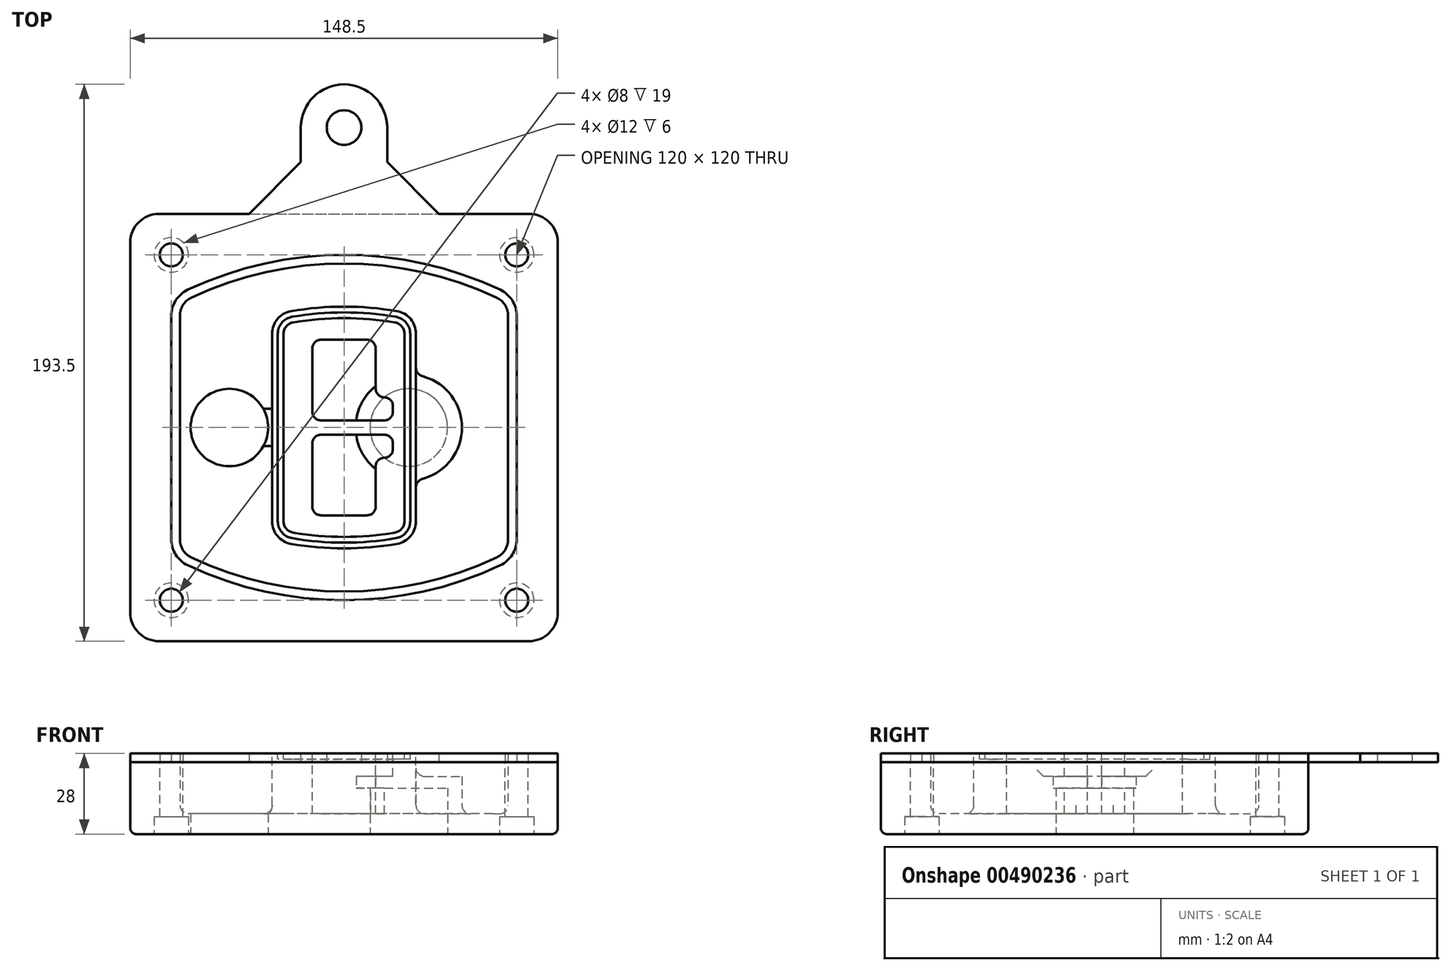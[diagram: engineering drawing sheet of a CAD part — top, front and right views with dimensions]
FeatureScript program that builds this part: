
annotation { "Feature Type Name" : "Feature", "Feature Type Description" : "" }
export const myFeature = defineFeature(function(context is Context, id is Id, definition is map)
    precondition{}
    {
        {
            var Q0;
            Q0=qCreatedBy(makeId("Top.planeOp"),FACE);
            var sketch = newSketch(context, id + "F0", { "sketchPlane" : qUnion([Q0])});
            skPoint(sketch, "E0.rect.middle", {"position": v(0, 0) * mm});
            skLineSegment(sketch, "E1.bottom", {"start": v(-64.25, -74.25) * mm, "end": v(64.25, -74.25) * mm});
            skLineSegment(sketch, "E1.top", {"start": v(-64.25, 74.25) * mm, "end": v(64.25, 74.25) * mm});
            skLineSegment(sketch, "E1.left", {"start": v(-74.25, -64.25) * mm, "end": v(-74.25, 64.25) * mm});
            skLineSegment(sketch, "E1.right", {"start": v(74.25, -64.25) * mm, "end": v(74.25, 64.25) * mm});
            skLineSegment(sketch, "E2", {"start": v(-74.25, 74.25) * mm, "end": v(74.25, -74.25) * mm, "construction": true});
            skLineSegment(sketch, "E3", {"start": v(74.25, 74.25) * mm, "end": v(-74.25, -74.25) * mm, "construction": true});
            skCircle(sketch, "E4", {"center": v(-60, 60) * mm, "radius": 4 * mm});
            skCircle(sketch, "E5", {"center": v(60, 60) * mm, "radius": 4 * mm});
            skCircle(sketch, "E6", {"center": v(60, -60) * mm, "radius": 4 * mm});
            skCircle(sketch, "E7", {"center": v(-60, -60) * mm, "radius": 4 * mm});
            skLineSegment(sketch, "E8", {"start": v(-60, 60) * mm, "end": v(60, 60) * mm, "construction": true});
            skLineSegment(sketch, "E9", {"start": v(60, 60) * mm, "end": v(60, -60) * mm, "construction": true});
            skLineSegment(sketch, "E10", {"start": v(60, -60) * mm, "end": v(-60, -60) * mm, "construction": true});
            skLineSegment(sketch, "E11", {"start": v(-60, -60) * mm, "end": v(-60, 60) * mm, "construction": true});
            skLineSegment(sketch, "E12", {"start": v(-60, 38.83) * mm, "end": v(-60, -38.83) * mm});
            skLineSegment(sketch, "E13", {"start": v(60, 38.83) * mm, "end": v(60, -38.83) * mm});
            skArc(sketch, "E14", {"start": v(54.26, 47.88) * mm, "mid": v(0, 60) * mm, "end": v(-54.26, 47.88) * mm});
            skArc(sketch, "E15", {"start": v(-54.26, -47.88) * mm, "mid": v(0, -60) * mm, "end": v(54.26, -47.88) * mm});
            skLineSegment(sketch, "E16", {"start": v(-60, 0) * mm, "end": v(60, 0) * mm, "construction": true});
            skPoint(sketch, "E17.visualSharp", {"position": v(-60, -45) * mm});
            skArc(sketch, "E17.filletArc", {"start": v(-60, -38.83) * mm, "mid": v(-58.44, -44.2) * mm, "end": v(-54.26, -47.88) * mm});
            skPoint(sketch, "E18.visualSharp", {"position": v(-60, 45) * mm});
            skArc(sketch, "E18.filletArc", {"start": v(-54.26, 47.88) * mm, "mid": v(-58.44, 44.2) * mm, "end": v(-60, 38.83) * mm});
            skPoint(sketch, "E19.visualSharp", {"position": v(60, 45) * mm});
            skArc(sketch, "E19.filletArc", {"start": v(60, 38.83) * mm, "mid": v(58.44, 44.2) * mm, "end": v(54.26, 47.88) * mm});
            skPoint(sketch, "E20.visualSharp", {"position": v(60, -45) * mm});
            skArc(sketch, "E20.filletArc", {"start": v(54.26, -47.88) * mm, "mid": v(58.44, -44.2) * mm, "end": v(60, -38.83) * mm});
            skPoint(sketch, "E21.visualSharp", {"position": v(-74.25, 74.25) * mm});
            skArc(sketch, "E21.filletArc", {"start": v(-64.25, 74.25) * mm, "mid": v(-71.32, 71.32) * mm, "end": v(-74.25, 64.25) * mm});
            skPoint(sketch, "E22.visualSharp", {"position": v(74.25, 74.25) * mm});
            skArc(sketch, "E22.filletArc", {"start": v(74.25, 64.25) * mm, "mid": v(71.32, 71.32) * mm, "end": v(64.25, 74.25) * mm});
            skPoint(sketch, "E23.visualSharp", {"position": v(74.25, -74.25) * mm});
            skArc(sketch, "E23.filletArc", {"start": v(64.25, -74.25) * mm, "mid": v(71.32, -71.32) * mm, "end": v(74.25, -64.25) * mm});
            skPoint(sketch, "E24.visualSharp", {"position": v(-74.25, -74.25) * mm});
            skArc(sketch, "E24.filletArc", {"start": v(-74.25, -64.25) * mm, "mid": v(-71.32, -71.32) * mm, "end": v(-64.25, -74.25) * mm});
            skArc(sketch, "E25.0", {"start": v(57, 38.83) * mm, "mid": v(55.9, 42.58) * mm, "end": v(52.98, 45.17) * mm});
            skLineSegment(sketch, "E25.1", {"start": v(57, 38.83) * mm, "end": v(57, -38.83) * mm});
            skArc(sketch, "E25.2", {"start": v(52.98, -45.17) * mm, "mid": v(55.9, -42.58) * mm, "end": v(57, -38.83) * mm});
            skArc(sketch, "E25.3", {"start": v(-52.98, -45.17) * mm, "mid": v(0, -57) * mm, "end": v(52.98, -45.17) * mm});
            skArc(sketch, "E25.4", {"start": v(-57, -38.83) * mm, "mid": v(-55.9, -42.58) * mm, "end": v(-52.98, -45.17) * mm});
            skArc(sketch, "E25.5", {"start": v(52.98, 45.17) * mm, "mid": v(0, 57) * mm, "end": v(-52.98, 45.17) * mm});
            skLineSegment(sketch, "E25.6", {"start": v(-57, 38.83) * mm, "end": v(-57, -38.83) * mm});
            skArc(sketch, "E25.7", {"start": v(-52.98, 45.17) * mm, "mid": v(-55.9, 42.58) * mm, "end": v(-57, 38.83) * mm});
            skArc(sketch, "E26.0", {"start": v(-55.96, 51.5) * mm, "mid": v(-61.82, 46.33) * mm, "end": v(-64, 38.83) * mm});
            skArc(sketch, "E26.1", {"start": v(55.96, 51.5) * mm, "mid": v(0, 64) * mm, "end": v(-55.96, 51.5) * mm});
            skArc(sketch, "E26.2", {"start": v(64, 38.83) * mm, "mid": v(61.82, 46.33) * mm, "end": v(55.96, 51.5) * mm});
            skLineSegment(sketch, "E26.3", {"start": v(64, 38.83) * mm, "end": v(64, -38.83) * mm});
            skArc(sketch, "E26.4", {"start": v(55.96, -51.5) * mm, "mid": v(61.82, -46.33) * mm, "end": v(64, -38.83) * mm});
            skLineSegment(sketch, "E26.5", {"start": v(-64, 38.83) * mm, "end": v(-64, -38.83) * mm});
            skArc(sketch, "E26.6", {"start": v(-55.96, -51.5) * mm, "mid": v(0, -64) * mm, "end": v(55.96, -51.5) * mm});
            skArc(sketch, "E26.7", {"start": v(-64, -38.83) * mm, "mid": v(-61.82, -46.33) * mm, "end": v(-55.96, -51.5) * mm});
            skSolve(sketch);
        }
        {
            var Q0;
            Q0=makeQuery(id+"F0.imprint","IMPRINT",FACE,{"disambiguationData":[TD([[makeQuery(id+"F0.imprint","IMPRINT",EDGE,{"derivedFrom":sQuery(id+"F0.wireOp",EDGE,"E1.bottom")}),1.0]])]});
            var Q1;
            Q1=makeQuery(id+"F0.imprint","IMPRINT",FACE,{"disambiguationData":[TD([[makeQuery(id+"F0.imprint","IMPRINT",EDGE,{"derivedFrom":sQuery(id+"F0.wireOp",EDGE,"E12")}),1.0]])]});
            var Q2;
            Q2=makeQuery(id+"F0.imprint","IMPRINT",FACE,{"disambiguationData":[TD([[makeQuery(id+"F0.imprint","IMPRINT",EDGE,{"derivedFrom":sQuery(id+"F0.wireOp",EDGE,"E25.0")}),1.0]])]});
            var Q3;
            Q3=makeQuery(id+"F0.imprint","IMPRINT",FACE,{"disambiguationData":[TD([[makeQuery(id+"F0.imprint","IMPRINT",EDGE,{"derivedFrom":sQuery(id+"F0.wireOp",EDGE,"E12")}),-1.0]])]});
            extrude(context, id + "F1", {"entities" : qUnion([Q0, Q1, Q2, Q3]), "oppositeDirection" : true, "depth" : 25 * mm});
        }
        {
            var Q0;
            Q0=makeQuery(id+"F0.imprint","IMPRINT",FACE,{"disambiguationData":[TD([[makeQuery(id+"F0.imprint","IMPRINT",EDGE,{"derivedFrom":sQuery(id+"F0.wireOp",EDGE,"E12")}),1.0]])]});
            extrude(context, id + "F2", {"entities" : qUnion([Q0]), "operationType" : NewBodyOperationType.ADD, "depth" : 3 * mm});
        }
        {
            var Q0;
            Q0=makeQuery(id+"F0.imprint","IMPRINT",FACE,{"disambiguationData":[TD([[makeQuery(id+"F0.imprint","IMPRINT",EDGE,{"derivedFrom":sQuery(id+"F0.wireOp",EDGE,"E25.0")}),1.0]])]});
            extrude(context, id + "F3", {"entities" : qUnion([Q0]), "operationType" : NewBodyOperationType.REMOVE, "oppositeDirection" : true, "depth" : 18 * mm});
        }
        {
            var Q0;
            Q0=makeQuery(id+"F2.opExtrude","CAP_FACE",FACE,{"disambiguationData":[OSD([sQuery(id+"F0.wireOp",EDGE,"E12"),sQuery(id+"F0.wireOp",EDGE,"E13"),sQuery(id+"F0.wireOp",EDGE,"E14"),sQuery(id+"F0.wireOp",EDGE,"E15"),sQuery(id+"F0.wireOp",EDGE,"E17.filletArc"),sQuery(id+"F0.wireOp",EDGE,"E18.filletArc"),sQuery(id+"F0.wireOp",EDGE,"E19.filletArc"),sQuery(id+"F0.wireOp",EDGE,"E20.filletArc"),sQuery(id+"F0.wireOp",EDGE,"E25.0"),sQuery(id+"F0.wireOp",EDGE,"E25.1"),sQuery(id+"F0.wireOp",EDGE,"E25.2"),sQuery(id+"F0.wireOp",EDGE,"E25.3"),sQuery(id+"F0.wireOp",EDGE,"E25.4"),sQuery(id+"F0.wireOp",EDGE,"E25.5"),sQuery(id+"F0.wireOp",EDGE,"E25.6"),sQuery(id+"F0.wireOp",EDGE,"E25.7")])],"isStart":false});
            var sketch = newSketch(context, id + "F4", { "sketchPlane" : qUnion([Q0])});
            skArc(sketch, "E27.0", {"start": v(-18.34, -40.45) * mm, "mid": v(0, -42) * mm, "end": v(18.34, -40.45) * mm});
            skArc(sketch, "E28.0", {"start": v(18.34, 40.45) * mm, "mid": v(0, 42) * mm, "end": v(-18.34, 40.45) * mm});
            skLineSegment(sketch, "E29", {"start": v(-25, 32.57) * mm, "end": v(-25, -32.57) * mm});
            skLineSegment(sketch, "E30", {"start": v(25, 32.57) * mm, "end": v(25, -32.57) * mm});
            skLineSegment(sketch, "E31", {"start": v(-25, 39.1) * mm, "end": v(25, 39.1) * mm, "construction": true});
            skLineSegment(sketch, "E32", {"start": v(-25, -39.1) * mm, "end": v(25, -39.1) * mm, "construction": true});
            skPoint(sketch, "E33.visualSharp", {"position": v(-25, 39.1) * mm});
            skArc(sketch, "E33.filletArc", {"start": v(-18.34, 40.45) * mm, "mid": v(-23.11, 37.73) * mm, "end": v(-25, 32.57) * mm});
            skPoint(sketch, "E34.visualSharp", {"position": v(25, 39.1) * mm});
            skArc(sketch, "E34.filletArc", {"start": v(25, 32.57) * mm, "mid": v(23.11, 37.73) * mm, "end": v(18.34, 40.45) * mm});
            skPoint(sketch, "E35.visualSharp", {"position": v(25, -39.1) * mm});
            skArc(sketch, "E35.filletArc", {"start": v(18.34, -40.45) * mm, "mid": v(23.11, -37.73) * mm, "end": v(25, -32.57) * mm});
            skPoint(sketch, "E36.visualSharp", {"position": v(-25, -39.1) * mm});
            skArc(sketch, "E36.filletArc", {"start": v(-25, -32.57) * mm, "mid": v(-23.11, -37.73) * mm, "end": v(-18.34, -40.45) * mm});
            skArc(sketch, "E37.0", {"start": v(52.98, 45.17) * mm, "mid": v(0, 57) * mm, "end": v(-52.98, 45.17) * mm});
            skArc(sketch, "E37.1", {"start": v(-52.98, 45.17) * mm, "mid": v(-55.9, 42.58) * mm, "end": v(-57, 38.83) * mm});
            skLineSegment(sketch, "E37.2", {"start": v(-57, 38.83) * mm, "end": v(-57, -38.83) * mm});
            skArc(sketch, "E37.3", {"start": v(-57, -38.83) * mm, "mid": v(-55.9, -42.58) * mm, "end": v(-52.98, -45.17) * mm});
            skArc(sketch, "E37.4", {"start": v(-52.98, -45.17) * mm, "mid": v(0, -57) * mm, "end": v(52.98, -45.17) * mm});
            skArc(sketch, "E37.5", {"start": v(52.98, -45.17) * mm, "mid": v(55.9, -42.58) * mm, "end": v(57, -38.83) * mm});
            skLineSegment(sketch, "E37.6", {"start": v(57, 38.83) * mm, "end": v(57, -38.83) * mm});
            skArc(sketch, "E37.7", {"start": v(57, 38.83) * mm, "mid": v(55.9, 42.58) * mm, "end": v(52.98, 45.17) * mm});
            skLineSegment(sketch, "E38.0", {"start": v(23, 32.57) * mm, "end": v(23, -32.57) * mm});
            skArc(sketch, "E38.1", {"start": v(18, -38.48) * mm, "mid": v(21.58, -36.44) * mm, "end": v(23, -32.57) * mm});
            skArc(sketch, "E38.2", {"start": v(-18, -38.48) * mm, "mid": v(0, -40) * mm, "end": v(18, -38.48) * mm});
            skArc(sketch, "E38.3", {"start": v(-23, -32.57) * mm, "mid": v(-21.58, -36.44) * mm, "end": v(-18, -38.48) * mm});
            skLineSegment(sketch, "E38.4", {"start": v(-23, 32.57) * mm, "end": v(-23, -32.57) * mm});
            skArc(sketch, "E38.5", {"start": v(23, 32.57) * mm, "mid": v(21.58, 36.44) * mm, "end": v(18, 38.48) * mm});
            skArc(sketch, "E38.6", {"start": v(-18, 38.48) * mm, "mid": v(-21.58, 36.44) * mm, "end": v(-23, 32.57) * mm});
            skArc(sketch, "E38.7", {"start": v(18, 38.48) * mm, "mid": v(0, 40) * mm, "end": v(-18, 38.48) * mm});
            skArc(sketch, "E39.0", {"start": v(21, 32.57) * mm, "mid": v(20.06, 35.15) * mm, "end": v(17.67, 36.5) * mm});
            skLineSegment(sketch, "E39.1", {"start": v(21, 32.57) * mm, "end": v(21, -32.57) * mm});
            skArc(sketch, "E39.2", {"start": v(17.67, -36.5) * mm, "mid": v(20.06, -35.15) * mm, "end": v(21, -32.57) * mm});
            skArc(sketch, "E39.3", {"start": v(-17.67, -36.5) * mm, "mid": v(0, -38) * mm, "end": v(17.67, -36.5) * mm});
            skArc(sketch, "E39.4", {"start": v(-21, -32.57) * mm, "mid": v(-20.06, -35.15) * mm, "end": v(-17.67, -36.5) * mm});
            skArc(sketch, "E39.5", {"start": v(17.67, 36.5) * mm, "mid": v(0, 38) * mm, "end": v(-17.67, 36.5) * mm});
            skLineSegment(sketch, "E39.6", {"start": v(-21, 32.57) * mm, "end": v(-21, -32.57) * mm});
            skArc(sketch, "E39.7", {"start": v(-17.67, 36.5) * mm, "mid": v(-20.06, 35.15) * mm, "end": v(-21, 32.57) * mm});
            skLineSegment(sketch, "E40", {"start": v(-25, 0) * mm, "end": v(25, 0) * mm, "construction": true});
            skLineSegment(sketch, "E41", {"start": v(-11, 5.5) * mm, "end": v(-11, 27.5) * mm});
            skLineSegment(sketch, "E42", {"start": v(-8, 30.5) * mm, "end": v(8, 30.5) * mm});
            skLineSegment(sketch, "E43", {"start": v(11, 27.5) * mm, "end": v(11, 13.5) * mm});
            skLineSegment(sketch, "E44", {"start": v(14, 10.5) * mm, "end": v(14, 10.5) * mm});
            skLineSegment(sketch, "E45", {"start": v(17, 7.5) * mm, "end": v(17, 5.5) * mm});
            skLineSegment(sketch, "E46", {"start": v(14, 2.5) * mm, "end": v(-8, 2.5) * mm});
            skPoint(sketch, "E47.visualSharp", {"position": v(-11, 30.5) * mm});
            skArc(sketch, "E47.filletArc", {"start": v(-8, 30.5) * mm, "mid": v(-10.12, 29.62) * mm, "end": v(-11, 27.5) * mm});
            skPoint(sketch, "E48.visualSharp", {"position": v(11, 30.5) * mm});
            skArc(sketch, "E48.filletArc", {"start": v(11, 27.5) * mm, "mid": v(10.12, 29.62) * mm, "end": v(8, 30.5) * mm});
            skPoint(sketch, "E49.visualSharp", {"position": v(11, 10.5) * mm});
            skArc(sketch, "E49.filletArc", {"start": v(11, 13.5) * mm, "mid": v(11.88, 11.38) * mm, "end": v(14, 10.5) * mm});
            skPoint(sketch, "E50.visualSharp", {"position": v(17, 10.5) * mm});
            skArc(sketch, "E50.filletArc", {"start": v(17, 7.5) * mm, "mid": v(16.12, 9.62) * mm, "end": v(14, 10.5) * mm});
            skPoint(sketch, "E51.visualSharp", {"position": v(17, 2.5) * mm});
            skArc(sketch, "E51.filletArc", {"start": v(14, 2.5) * mm, "mid": v(16.12, 3.38) * mm, "end": v(17, 5.5) * mm});
            skPoint(sketch, "E52.visualSharp", {"position": v(-11, 2.5) * mm});
            skArc(sketch, "E52.filletArc", {"start": v(-11, 5.5) * mm, "mid": v(-10.12, 3.38) * mm, "end": v(-8, 2.5) * mm});
            skLineSegment(sketch, "E53.0.MirrorCS", {"start": v(14, -2.5) * mm, "end": v(-8, -2.5) * mm});
            skArc(sketch, "E54.0.MirrorCS", {"start": v(-11, -5.5) * mm, "mid": v(-10.12, -3.38) * mm, "end": v(-8, -2.5) * mm});
            skLineSegment(sketch, "E55.0.MirrorCS", {"start": v(-11, -5.5) * mm, "end": v(-11, -27.5) * mm});
            skArc(sketch, "E56.0.MirrorCS", {"start": v(-8, -30.5) * mm, "mid": v(-10.12, -29.62) * mm, "end": v(-11, -27.5) * mm});
            skLineSegment(sketch, "E57.0.MirrorCS", {"start": v(-8, -30.5) * mm, "end": v(8, -30.5) * mm});
            skArc(sketch, "E58.0.MirrorCS", {"start": v(11, -27.5) * mm, "mid": v(10.12, -29.62) * mm, "end": v(8, -30.5) * mm});
            skLineSegment(sketch, "E59.0.MirrorCS", {"start": v(11, -27.5) * mm, "end": v(11, -13.5) * mm});
            skArc(sketch, "E60.0.MirrorCS", {"start": v(11, -13.5) * mm, "mid": v(11.88, -11.38) * mm, "end": v(14, -10.5) * mm});
            skArc(sketch, "E61.0.MirrorCS", {"start": v(17, -7.5) * mm, "mid": v(16.12, -9.62) * mm, "end": v(14, -10.5) * mm});
            skLineSegment(sketch, "E62.0.MirrorCS", {"start": v(17, -7.5) * mm, "end": v(17, -5.5) * mm});
            skArc(sketch, "E63.0.MirrorCS", {"start": v(14, -2.5) * mm, "mid": v(16.12, -3.38) * mm, "end": v(17, -5.5) * mm});
            skSolve(sketch);
        }
        {
            var Q0;
            Q0=makeQuery(id+"F4.imprint","IMPRINT",FACE,{"disambiguationData":[TD([[makeQuery(id+"F4.imprint","IMPRINT",EDGE,{"derivedFrom":sQuery(id+"F4.wireOp",EDGE,"E27.0")}),1.0]])]});
            var Q1;
            Q1=makeQuery(id+"F4.imprint","IMPRINT",FACE,{"disambiguationData":[TD([[makeQuery(id+"F4.imprint","IMPRINT",EDGE,{"derivedFrom":sQuery(id+"F4.wireOp",EDGE,"E38.0")}),-1.0]])]});
            var Q2;
            Q2=makeQuery(id+"F4.imprint","IMPRINT",FACE,{"disambiguationData":[TD([[makeQuery(id+"F4.imprint","IMPRINT",EDGE,{"derivedFrom":sQuery(id+"F4.wireOp",EDGE,"E39.0")}),1.0]])]});
            extrude(context, id + "F5", {"entities" : qUnion([Q0, Q1, Q2]), "operationType" : NewBodyOperationType.ADD, "endBound" : BoundingType.UP_TO_NEXT, "oppositeDirection" : true, "depth" : 25 * mm});
        }
        {
            var Q0;
            Q0=makeQuery(id+"F4.imprint","IMPRINT",FACE,{"disambiguationData":[TD([[makeQuery(id+"F4.imprint","IMPRINT",EDGE,{"derivedFrom":sQuery(id+"F4.wireOp",EDGE,"E38.0")}),-1.0]])]});
            extrude(context, id + "F6", {"entities" : qUnion([Q0]), "operationType" : NewBodyOperationType.REMOVE, "oppositeDirection" : true, "depth" : 2 * mm});
        }
        {
            var Q0;
            Q0=makeQuery(id+"F1.opExtrude","CAP_FACE",FACE,{"disambiguationData":[OSD([sQuery(id+"F0.wireOp",EDGE,"E1.bottom"),sQuery(id+"F0.wireOp",EDGE,"E1.top"),sQuery(id+"F0.wireOp",EDGE,"E1.left"),sQuery(id+"F0.wireOp",EDGE,"E1.right"),sQuery(id+"F0.wireOp",EDGE,"E4"),sQuery(id+"F0.wireOp",EDGE,"E5"),sQuery(id+"F0.wireOp",EDGE,"E6"),sQuery(id+"F0.wireOp",EDGE,"E7"),sQuery(id+"F0.wireOp",EDGE,"E21.filletArc"),sQuery(id+"F0.wireOp",EDGE,"E22.filletArc"),sQuery(id+"F0.wireOp",EDGE,"E23.filletArc"),sQuery(id+"F0.wireOp",EDGE,"E24.filletArc")])],"isStart":false});
            var sketch = newSketch(context, id + "F7", { "sketchPlane" : qUnion([Q0])});
            skCircle(sketch, "E64", {"center": v(22.5, 0) * mm, "radius": 13.47 * mm});
            skCircle(sketch, "E65", {"center": v(-39.81, 0) * mm, "radius": 13.47 * mm});
            skLineSegment(sketch, "E66", {"start": v(74.25, 0) * mm, "end": v(-74.25, 0) * mm});
            skCircle(sketch, "E67", {"center": v(22.5, 0) * mm, "radius": 18.47 * mm});
            skCircle(sketch, "E68", {"center": v(60, -60) * mm, "radius": 6 * mm});
            skCircle(sketch, "E69", {"center": v(-60, -60) * mm, "radius": 6 * mm});
            skCircle(sketch, "E70", {"center": v(-60, 60) * mm, "radius": 6 * mm});
            skCircle(sketch, "E71", {"center": v(60, 60) * mm, "radius": 6 * mm});
            skSolve(sketch);
        }
        {
            var Q0;
            {var subQ1=sQuery(id+"F7.wireOp",EDGE,"E66");var subQ4=sQuery(id+"F7.wireOp",EDGE,"E64");var subQ6=makeQuery(id+"F7.imprint","INTERSECT",VERTEX,{"disambiguationData":[OD(0.0)],"derivedFrom":[subQ4,subQ1]});Q0=makeQuery(id+"F7.imprint","IMPRINT",FACE,{"disambiguationData":[TD([[makeQuery(id+"F7.imprint","IMPRINT",EDGE,{"disambiguationData":[TD([[subQ6,-1.0]])],"derivedFrom":subQ4}),-1.0]])]});}
            var Q1;
            {var subQ0=sQuery(id+"F7.wireOp",EDGE,"E66");var subQ1=sQuery(id+"F7.wireOp",EDGE,"E64");var subQ3=makeQuery(id+"F7.imprint","INTERSECT",VERTEX,{"disambiguationData":[OD(0.0)],"derivedFrom":[subQ1,subQ0]});Q1=makeQuery(id+"F7.imprint","IMPRINT",FACE,{"disambiguationData":[TD([[makeQuery(id+"F7.imprint","IMPRINT",EDGE,{"disambiguationData":[TD([[subQ3,-1.0]])],"derivedFrom":subQ1}),1.0]])]});}
            var Q2;
            {var subQ0=sQuery(id+"F7.wireOp",EDGE,"E66");var subQ1=sQuery(id+"F7.wireOp",EDGE,"E64");var subQ3=makeQuery(id+"F7.imprint","INTERSECT",VERTEX,{"disambiguationData":[OD(0.0)],"derivedFrom":[subQ1,subQ0]});Q2=makeQuery(id+"F7.imprint","IMPRINT",FACE,{"disambiguationData":[TD([[makeQuery(id+"F7.imprint","IMPRINT",EDGE,{"disambiguationData":[TD([[subQ3,1.0]])],"derivedFrom":subQ1}),1.0]])]});}
            var Q3;
            {var subQ1=sQuery(id+"F7.wireOp",EDGE,"E66");var subQ4=sQuery(id+"F7.wireOp",EDGE,"E64");var subQ6=makeQuery(id+"F7.imprint","INTERSECT",VERTEX,{"disambiguationData":[OD(0.0)],"derivedFrom":[subQ4,subQ1]});Q3=makeQuery(id+"F7.imprint","IMPRINT",FACE,{"disambiguationData":[TD([[makeQuery(id+"F7.imprint","IMPRINT",EDGE,{"disambiguationData":[TD([[subQ6,1.0]])],"derivedFrom":subQ4}),-1.0]])]});}
            extrude(context, id + "F8", {"entities" : qUnion([Q0, Q1, Q2, Q3]), "operationType" : NewBodyOperationType.ADD, "oppositeDirection" : true, "depth" : 20 * mm});
        }
        {
            var Q0;
            {var subQ0=sQuery(id+"F7.wireOp",EDGE,"E66");var subQ1=sQuery(id+"F7.wireOp",EDGE,"E64");var subQ3=makeQuery(id+"F7.imprint","INTERSECT",VERTEX,{"disambiguationData":[OD(0.0)],"derivedFrom":[subQ1,subQ0]});Q0=makeQuery(id+"F7.imprint","IMPRINT",FACE,{"disambiguationData":[TD([[makeQuery(id+"F7.imprint","IMPRINT",EDGE,{"disambiguationData":[TD([[subQ3,-1.0]])],"derivedFrom":subQ1}),1.0]])]});}
            var Q1;
            {var subQ0=sQuery(id+"F7.wireOp",EDGE,"E66");var subQ1=sQuery(id+"F7.wireOp",EDGE,"E64");var subQ3=makeQuery(id+"F7.imprint","INTERSECT",VERTEX,{"disambiguationData":[OD(0.0)],"derivedFrom":[subQ1,subQ0]});Q1=makeQuery(id+"F7.imprint","IMPRINT",FACE,{"disambiguationData":[TD([[makeQuery(id+"F7.imprint","IMPRINT",EDGE,{"disambiguationData":[TD([[subQ3,1.0]])],"derivedFrom":subQ1}),1.0]])]});}
            extrude(context, id + "F9", {"entities" : qUnion([Q0, Q1]), "operationType" : NewBodyOperationType.REMOVE, "oppositeDirection" : true, "depth" : 16 * mm});
        }
        {
            var Q0;
            {var subQ0=sQuery(id+"F7.wireOp",EDGE,"E66");var subQ1=sQuery(id+"F7.wireOp",EDGE,"E65");var subQ3=makeQuery(id+"F7.imprint","INTERSECT",VERTEX,{"disambiguationData":[OD(0.0)],"derivedFrom":[subQ1,subQ0]});Q0=makeQuery(id+"F7.imprint","IMPRINT",FACE,{"disambiguationData":[TD([[makeQuery(id+"F7.imprint","IMPRINT",EDGE,{"disambiguationData":[TD([[subQ3,-1.0]])],"derivedFrom":subQ1}),1.0]])]});}
            var Q1;
            {var subQ0=sQuery(id+"F7.wireOp",EDGE,"E66");var subQ1=sQuery(id+"F7.wireOp",EDGE,"E65");var subQ3=makeQuery(id+"F7.imprint","INTERSECT",VERTEX,{"disambiguationData":[OD(0.0)],"derivedFrom":[subQ1,subQ0]});Q1=makeQuery(id+"F7.imprint","IMPRINT",FACE,{"disambiguationData":[TD([[makeQuery(id+"F7.imprint","IMPRINT",EDGE,{"disambiguationData":[TD([[subQ3,1.0]])],"derivedFrom":subQ1}),1.0]])]});}
            extrude(context, id + "F10", {"entities" : qUnion([Q0, Q1]), "operationType" : NewBodyOperationType.REMOVE, "oppositeDirection" : true, "depth" : 25 * mm});
        }
        {
            var Q0;
            Q0=makeQuery(id+"F7.imprint","IMPRINT",FACE,{"disambiguationData":[TD([[makeQuery(id+"F7.imprint","IMPRINT",EDGE,{"derivedFrom":sQuery(id+"F7.wireOp",EDGE,"E68")}),1.0]])]});
            var Q1;
            Q1=makeQuery(id+"F7.imprint","IMPRINT",FACE,{"disambiguationData":[TD([[makeQuery(id+"F7.imprint","IMPRINT",EDGE,{"derivedFrom":makeQuery(id+"F1.opExtrude","CAP_EDGE",EDGE,{"disambiguationData":[OSD([sQuery(id+"F0.wireOp",EDGE,"E5")])],"isStart":false})}),-1.0]])]});
            var Q2;
            Q2=makeQuery(id+"F7.imprint","IMPRINT",FACE,{"disambiguationData":[TD([[makeQuery(id+"F7.imprint","IMPRINT",EDGE,{"derivedFrom":sQuery(id+"F7.wireOp",EDGE,"E69")}),1.0]])]});
            var Q3;
            Q3=makeQuery(id+"F7.imprint","IMPRINT",FACE,{"disambiguationData":[TD([[makeQuery(id+"F7.imprint","IMPRINT",EDGE,{"derivedFrom":makeQuery(id+"F1.opExtrude","CAP_EDGE",EDGE,{"disambiguationData":[OSD([sQuery(id+"F0.wireOp",EDGE,"E4")])],"isStart":false})}),-1.0]])]});
            var Q4;
            Q4=makeQuery(id+"F7.imprint","IMPRINT",FACE,{"disambiguationData":[TD([[makeQuery(id+"F7.imprint","IMPRINT",EDGE,{"derivedFrom":sQuery(id+"F7.wireOp",EDGE,"E70")}),1.0]])]});
            var Q5;
            Q5=makeQuery(id+"F7.imprint","IMPRINT",FACE,{"disambiguationData":[TD([[makeQuery(id+"F7.imprint","IMPRINT",EDGE,{"derivedFrom":makeQuery(id+"F1.opExtrude","CAP_EDGE",EDGE,{"disambiguationData":[OSD([sQuery(id+"F0.wireOp",EDGE,"E7")])],"isStart":false})}),-1.0]])]});
            var Q6;
            Q6=makeQuery(id+"F7.imprint","IMPRINT",FACE,{"disambiguationData":[TD([[makeQuery(id+"F7.imprint","IMPRINT",EDGE,{"derivedFrom":sQuery(id+"F7.wireOp",EDGE,"E71")}),1.0]])]});
            var Q7;
            Q7=makeQuery(id+"F7.imprint","IMPRINT",FACE,{"disambiguationData":[TD([[makeQuery(id+"F7.imprint","IMPRINT",EDGE,{"derivedFrom":makeQuery(id+"F1.opExtrude","CAP_EDGE",EDGE,{"disambiguationData":[OSD([sQuery(id+"F0.wireOp",EDGE,"E6")])],"isStart":false})}),-1.0]])]});
            extrude(context, id + "F11", {"entities" : qUnion([Q0, Q1, Q2, Q3, Q4, Q5, Q6, Q7]), "operationType" : NewBodyOperationType.REMOVE, "oppositeDirection" : true, "depth" : 6 * mm});
        }
        {
            var Q0;
            Q0=makeQuery(id+"F9.boolean.opBoolean","COPY",FACE,{"derivedFrom":makeQuery(id+"F9.opExtrude","CAP_FACE",FACE,{"disambiguationData":[OSD([sQuery(id+"F7.wireOp",EDGE,"E64")])],"isStart":false})});
            var sketch = newSketch(context, id + "F12", { "sketchPlane" : qUnion([Q0])});
            skArc(sketch, "E72.0", {"start": v(11, 14.45) * mm, "mid": v(6.45, 9.13) * mm, "end": v(4.2, 2.5) * mm});
            skArc(sketch, "E72.1", {"start": v(4.2, -2.5) * mm, "mid": v(6.45, -9.13) * mm, "end": v(11, -14.45) * mm});
            skLineSegment(sketch, "E73", {"start": v(4.2, -2.5) * mm, "end": v(14, -2.5) * mm});
            skLineSegment(sketch, "E74.0", {"start": v(14, 2.5) * mm, "end": v(4.2, 2.5) * mm});
            skArc(sketch, "E74.1", {"start": v(14, 2.5) * mm, "mid": v(16.12, 3.38) * mm, "end": v(17, 5.5) * mm});
            skLineSegment(sketch, "E74.2", {"start": v(17, 7.5) * mm, "end": v(17, 5.5) * mm});
            skArc(sketch, "E74.3", {"start": v(17, 7.5) * mm, "mid": v(16.12, 9.62) * mm, "end": v(14, 10.5) * mm});
            skArc(sketch, "E74.4", {"start": v(11, 13.5) * mm, "mid": v(11.88, 11.38) * mm, "end": v(14, 10.5) * mm});
            skLineSegment(sketch, "E74.5", {"start": v(11, 14.45) * mm, "end": v(11, 13.5) * mm});
            skLineSegment(sketch, "E74.7", {"start": v(14, -2.5) * mm, "end": v(4.2, -2.5) * mm});
            skArc(sketch, "E74.8", {"start": v(14, -2.5) * mm, "mid": v(16.12, -3.38) * mm, "end": v(17, -5.5) * mm});
            skLineSegment(sketch, "E74.9", {"start": v(17, -7.5) * mm, "end": v(17, -5.5) * mm});
            skArc(sketch, "E74.10", {"start": v(17, -7.5) * mm, "mid": v(16.12, -9.62) * mm, "end": v(14, -10.5) * mm});
            skArc(sketch, "E74.11", {"start": v(11, -13.5) * mm, "mid": v(11.88, -11.38) * mm, "end": v(14, -10.5) * mm});
            skLineSegment(sketch, "E74.12", {"start": v(11, -14.45) * mm, "end": v(11, -13.5) * mm});
            skPoint(sketch, "E75.orphan", {"position": v(11, -27.5) * mm});
            skPoint(sketch, "E76.orphan", {"position": v(-8, -2.5) * mm});
            skPoint(sketch, "E77.orphan", {"position": v(-8, 2.5) * mm});
            skPoint(sketch, "E78.orphan", {"position": v(11, 27.5) * mm});
            skSolve(sketch);
        }
        {
            var Q0;
            {var subQ7=sQuery(id+"F12.wireOp",EDGE,"E72.0");var subQ14=sQuery(id+"F12.wireOp",EDGE,"E72.1");var subQ16=sQuery(id+"F12.wireOp",EDGE,"E74.1");var subQ18=sQuery(id+"F12.wireOp",EDGE,"E74.8");Q0=qUnion([makeQuery(id+"F12.imprint","IMPRINT",FACE,{"disambiguationData":[TD([[makeQuery(id+"F12.imprint","IMPRINT",EDGE,{"derivedFrom":subQ7}),1.0]])]}),makeQuery(id+"F12.imprint","IMPRINT",FACE,{"disambiguationData":[TD([[makeQuery(id+"F12.imprint","IMPRINT",EDGE,{"derivedFrom":subQ14}),1.0]])]}),makeQuery(id+"F12.imprint","IMPRINT",FACE,{"disambiguationData":[TD([[makeQuery(id+"F12.imprint","IMPRINT",EDGE,{"derivedFrom":subQ16}),1.0]])]}),makeQuery(id+"F12.imprint","IMPRINT",FACE,{"disambiguationData":[TD([[makeQuery(id+"F12.imprint","IMPRINT",EDGE,{"derivedFrom":subQ18}),-1.0]])]})]);}
            var Q1;
            Q1=makeQuery(id+"F5.boolean.opBoolean","SPLIT",FACE,{"disambiguationData":[TD([makeQuery(id+"F5.opExtrude","SWEPT_FACE",FACE,{"disambiguationData":[OSD([sQuery(id+"F4.wireOp",EDGE,"E41")])]})])],"derivedFrom":makeQuery(id+"F3.boolean.opBoolean","COPY",FACE,{"derivedFrom":makeQuery(id+"F3.opExtrude","CAP_FACE",FACE,{"disambiguationData":[OSD([sQuery(id+"F0.wireOp",EDGE,"E25.0"),sQuery(id+"F0.wireOp",EDGE,"E25.1"),sQuery(id+"F0.wireOp",EDGE,"E25.2"),sQuery(id+"F0.wireOp",EDGE,"E25.3"),sQuery(id+"F0.wireOp",EDGE,"E25.4"),sQuery(id+"F0.wireOp",EDGE,"E25.5"),sQuery(id+"F0.wireOp",EDGE,"E25.6"),sQuery(id+"F0.wireOp",EDGE,"E25.7")])],"isStart":false})})});
            extrude(context, id + "F13", {"entities" : qUnion([Q0]), "operationType" : NewBodyOperationType.REMOVE, "endBound" : BoundingType.UP_TO_SURFACE, "endBoundEntityFace" : qUnion([Q1]), "depth" : 25 * mm});
        }
        {
            var Q0;
            Q0=makeQuery(id+"F3.boolean.opBoolean","COPY",EDGE,{"derivedFrom":makeQuery(id+"F3.opExtrude","CAP_EDGE",EDGE,{"disambiguationData":[OSD([sQuery(id+"F0.wireOp",EDGE,"E25.6")])],"isStart":false})});
            var Q1;
            Q1=makeQuery(id+"F8.boolean.opBoolean","INTERSECT",EDGE,{"derivedFrom":[makeQuery(id+"F5.opExtrude","SWEPT_FACE",FACE,{"disambiguationData":[OSD([sQuery(id+"F4.wireOp",EDGE,"E30")])]}),makeQuery(id+"F8.opExtrude","CAP_FACE",FACE,{"disambiguationData":[OSD([sQuery(id+"F7.wireOp",EDGE,"E67")])],"isStart":false})]});
            var Q2;
            Q2=makeQuery(id+"F8.boolean.opBoolean","INTERSECT",EDGE,{"disambiguationData":[OD(1.0)],"derivedFrom":[makeQuery(id+"F5.opExtrude","SWEPT_FACE",FACE,{"disambiguationData":[OSD([sQuery(id+"F4.wireOp",EDGE,"E30")])]}),makeQuery(id+"F8.opExtrude","SWEPT_FACE",FACE,{"disambiguationData":[OSD([sQuery(id+"F7.wireOp",EDGE,"E67")])]})]});
            var Q3;
            {var subQ0=sQuery(id+"F4.wireOp",EDGE,"E30");Q3=makeQuery(id+"F8.boolean.opBoolean","SPLIT",EDGE,{"disambiguationData":[TD([makeQuery(id+"F5.opExtrude","SWEPT_FACE",FACE,{"disambiguationData":[OSD([sQuery(id+"F4.wireOp",EDGE,"E35.filletArc")])]})])],"derivedFrom":makeQuery(id+"F5.opExtrude","CAP_EDGE",EDGE,{"disambiguationData":[OSD([subQ0])],"isStart":false})});}
            var Q4;
            {var subQ0=sQuery(id+"F0.wireOp",EDGE,"E25.7");var subQ1=sQuery(id+"F0.wireOp",EDGE,"E25.1");var subQ2=sQuery(id+"F0.wireOp",EDGE,"E25.6");var subQ3=sQuery(id+"F0.wireOp",EDGE,"E25.5");var subQ4=sQuery(id+"F0.wireOp",EDGE,"E25.4");var subQ5=sQuery(id+"F0.wireOp",EDGE,"E25.0");var subQ6=sQuery(id+"F0.wireOp",EDGE,"E25.2");var subQ7=sQuery(id+"F0.wireOp",EDGE,"E25.3");Q4=makeQuery(id+"F8.boolean.opBoolean","INTERSECT",EDGE,{"derivedFrom":[makeQuery(id+"F5.boolean.opBoolean","SPLIT",FACE,{"disambiguationData":[TD([makeQuery(id+"F2.opExtrude","SWEPT_FACE",FACE,{"disambiguationData":[OSD([subQ5])]})])],"derivedFrom":makeQuery(id+"F3.boolean.opBoolean","COPY",FACE,{"derivedFrom":makeQuery(id+"F3.opExtrude","CAP_FACE",FACE,{"disambiguationData":[OSD([subQ5,subQ1,subQ6,subQ7,subQ4,subQ3,subQ2,subQ0])],"isStart":false})})}),makeQuery(id+"F8.opExtrude","SWEPT_FACE",FACE,{"disambiguationData":[OSD([sQuery(id+"F7.wireOp",EDGE,"E67")])]})]});}
            var Q5;
            Q5=makeQuery(id+"F8.boolean.opBoolean","INTERSECT",EDGE,{"disambiguationData":[OD(0.0)],"derivedFrom":[makeQuery(id+"F5.opExtrude","SWEPT_FACE",FACE,{"disambiguationData":[OSD([sQuery(id+"F4.wireOp",EDGE,"E30")])]}),makeQuery(id+"F8.opExtrude","SWEPT_FACE",FACE,{"disambiguationData":[OSD([sQuery(id+"F7.wireOp",EDGE,"E67")])]})]});
            fillet(context, id + "F14", {"entities" : qUnion([Q0, Q1, Q2, Q3, Q4, Q5]), "radius" : 3 * mm, "tangentPropagation" : true, "allowEdgeOverflow" : false});
        }
        {
            var Q0;
            Q0=makeQuery(id+"F1.opExtrude","CAP_EDGE",EDGE,{"disambiguationData":[OSD([sQuery(id+"F0.wireOp",EDGE,"E1.bottom")])],"isStart":false});
            fillet(context, id + "F15", {"entities" : qUnion([Q0]), "radius" : 2 * mm, "tangentPropagation" : true, "allowEdgeOverflow" : false});
        }
        {
            var Q0;
            {var subQ0=sQuery(id+"F0.wireOp",EDGE,"E21.filletArc");var subQ1=sQuery(id+"F0.wireOp",EDGE,"E7");var subQ2=sQuery(id+"F0.wireOp",EDGE,"E6");var subQ3=sQuery(id+"F0.wireOp",EDGE,"E5");var subQ4=sQuery(id+"F0.wireOp",EDGE,"E4");var subQ5=sQuery(id+"F0.wireOp",EDGE,"E22.filletArc");var subQ6=sQuery(id+"F0.wireOp",EDGE,"E1.bottom");var subQ7=sQuery(id+"F0.wireOp",EDGE,"E1.right");var subQ8=sQuery(id+"F0.wireOp",EDGE,"E1.top");var subQ9=sQuery(id+"F0.wireOp",EDGE,"E1.left");var subQ10=sQuery(id+"F0.wireOp",EDGE,"E23.filletArc");var subQ11=sQuery(id+"F0.wireOp",EDGE,"E24.filletArc");Q0=makeQuery(id+"F2.boolean.opBoolean","SPLIT",FACE,{"disambiguationData":[TD([makeQuery(id+"F1.opExtrude","SWEPT_FACE",FACE,{"disambiguationData":[OSD([subQ6])]})])],"derivedFrom":makeQuery(id+"F1.opExtrude","CAP_FACE",FACE,{"disambiguationData":[OSD([subQ6,subQ8,subQ9,subQ7,subQ4,subQ3,subQ2,subQ1,subQ0,subQ5,subQ10,subQ11])],"isStart":true})});}
            var sketch = newSketch(context, id + "F16", { "sketchPlane" : qUnion([Q0])});
            skLineSegment(sketch, "E79", {"start": v(0, 74.25) * mm, "end": v(0, 104.25) * mm, "construction": true});
            skArc(sketch, "E80", {"start": v(15, 104.25) * mm, "mid": v(0, 119.25) * mm, "end": v(-15, 104.25) * mm});
            skLineSegment(sketch, "E81", {"start": v(15, 104.25) * mm, "end": v(15, 92.25) * mm});
            skLineSegment(sketch, "E82", {"start": v(-15, 104.25) * mm, "end": v(-15, 92.25) * mm});
            skLineSegment(sketch, "E83", {"start": v(15, 92.25) * mm, "end": v(33, 74.25) * mm});
            skLineSegment(sketch, "E84", {"start": v(-15, 92.25) * mm, "end": v(-33, 74.25) * mm});
            skCircle(sketch, "E85", {"center": v(0, 104.25) * mm, "radius": 6 * mm});
            skLineSegment(sketch, "E86", {"start": v(-74.25, 0) * mm, "end": v(74.25, 0) * mm, "construction": true});
            skLineSegment(sketch, "E87.MirrorCS", {"start": v(0, -74.25) * mm, "end": v(0, -104.25) * mm, "construction": true});
            skArc(sketch, "E88.MirrorCS", {"start": v(15, -104.25) * mm, "mid": v(0, -119.25) * mm, "end": v(-15, -104.25) * mm});
            skLineSegment(sketch, "E89.MirrorCS", {"start": v(15, -104.25) * mm, "end": v(15, -92.25) * mm});
            skLineSegment(sketch, "E90.MirrorCS", {"start": v(-15, -104.25) * mm, "end": v(-15, -92.25) * mm});
            skLineSegment(sketch, "E91.MirrorCS", {"start": v(15, -92.25) * mm, "end": v(33, -74.25) * mm});
            skLineSegment(sketch, "E92.MirrorCS", {"start": v(-15, -92.25) * mm, "end": v(-33, -74.25) * mm});
            skCircle(sketch, "E93.MirrorC", {"center": v(0, -104.25) * mm, "radius": 6 * mm});
            skSolve(sketch);
        }
        {
            var Q0;
            Q0=makeQuery(id+"F16.imprint","IMPRINT",FACE,{"disambiguationData":[TD([[makeQuery(id+"F16.imprint","IMPRINT",EDGE,{"derivedFrom":sQuery(id+"F16.wireOp",EDGE,"E80")}),1.0]])]});
            var Q1;
            Q1=makeQuery(id+"F16.imprint","IMPRINT",FACE,{"disambiguationData":[TD([[makeQuery(id+"F16.imprint","IMPRINT",EDGE,{"derivedFrom":makeQuery(id+"F1.opExtrude","CAP_EDGE",EDGE,{"disambiguationData":[OSD([sQuery(id+"F0.wireOp",EDGE,"E1.left")])],"isStart":true})}),-1.0]])]});
            var Q2;
            Q2=makeQuery(id+"F16.imprint","IMPRINT",FACE,{"disambiguationData":[TD([[makeQuery(id+"F16.imprint","IMPRINT",EDGE,{"derivedFrom":sQuery(id+"F16.wireOp",EDGE,"E88.MirrorCS")}),-1.0]])]});
            var Q3;
            Q3=makeQuery(id+"F2.opExtrude","CAP_FACE",FACE,{"disambiguationData":[OSD([sQuery(id+"F0.wireOp",EDGE,"E12"),sQuery(id+"F0.wireOp",EDGE,"E13"),sQuery(id+"F0.wireOp",EDGE,"E14"),sQuery(id+"F0.wireOp",EDGE,"E15"),sQuery(id+"F0.wireOp",EDGE,"E17.filletArc"),sQuery(id+"F0.wireOp",EDGE,"E18.filletArc"),sQuery(id+"F0.wireOp",EDGE,"E19.filletArc"),sQuery(id+"F0.wireOp",EDGE,"E20.filletArc"),sQuery(id+"F0.wireOp",EDGE,"E25.0"),sQuery(id+"F0.wireOp",EDGE,"E25.1"),sQuery(id+"F0.wireOp",EDGE,"E25.2"),sQuery(id+"F0.wireOp",EDGE,"E25.3"),sQuery(id+"F0.wireOp",EDGE,"E25.4"),sQuery(id+"F0.wireOp",EDGE,"E25.5"),sQuery(id+"F0.wireOp",EDGE,"E25.6"),sQuery(id+"F0.wireOp",EDGE,"E25.7")])],"isStart":false});
            extrude(context, id + "F17", {"entities" : qUnion([Q0, Q1, Q2]), "endBound" : BoundingType.UP_TO_SURFACE, "endBoundEntityFace" : qUnion([Q3]), "depth" : 25 * mm});
        }
    });
